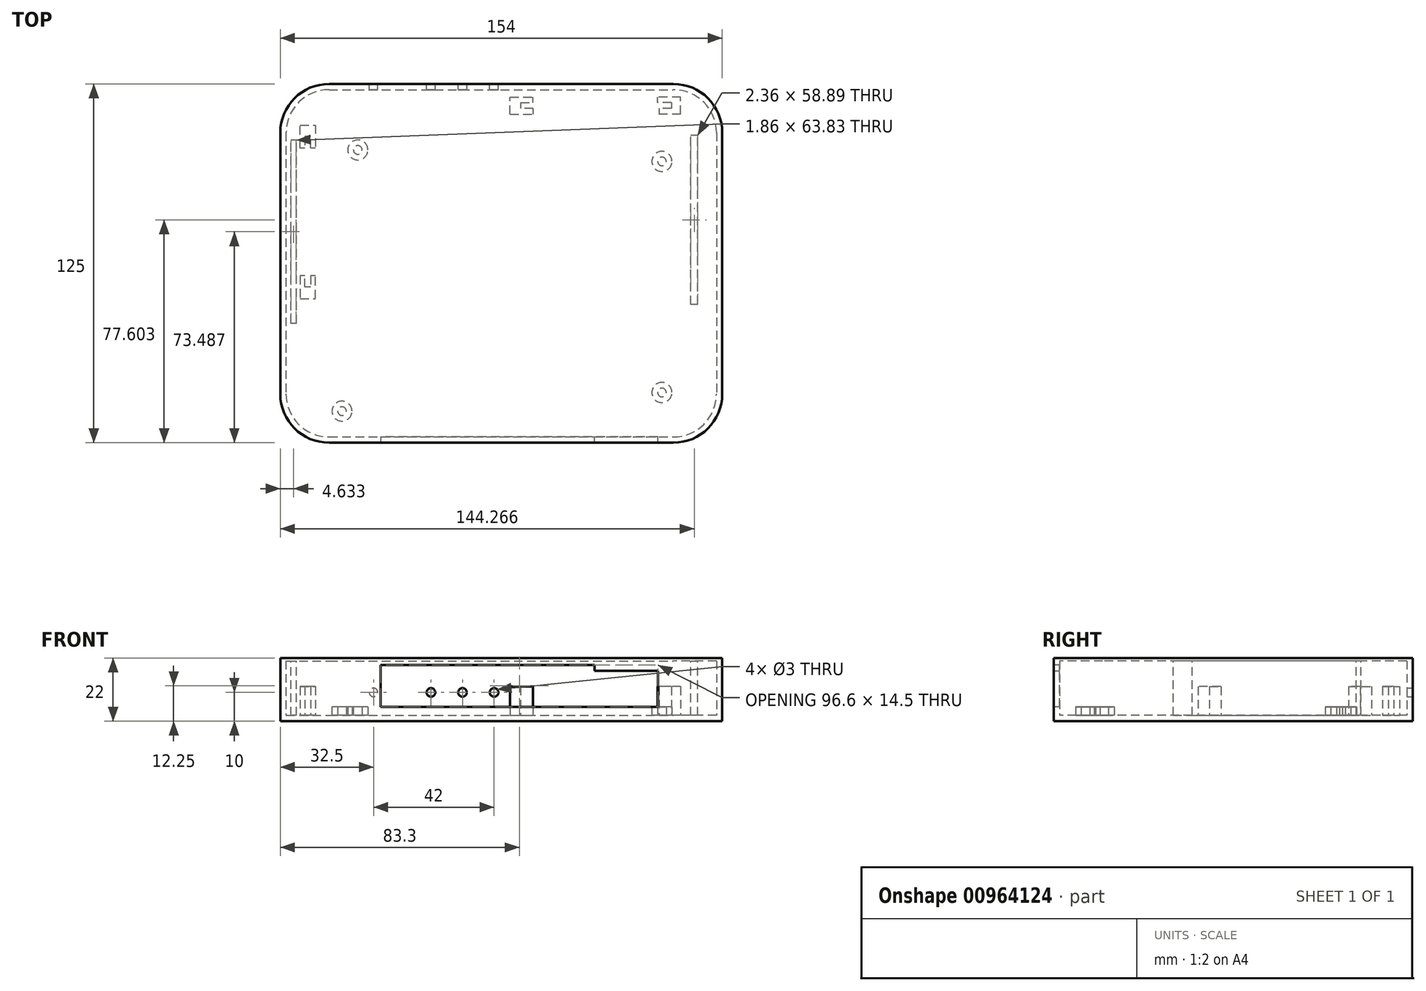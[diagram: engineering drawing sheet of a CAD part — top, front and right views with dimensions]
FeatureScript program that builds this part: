
annotation { "Feature Type Name" : "Feature", "Feature Type Description" : "" }
export const myFeature = defineFeature(function(context is Context, id is Id, definition is map)
    precondition{}
    {
        {
            var Q0;
            Q0=qCreatedBy(makeId("Top.planeOp"),FACE);
            var sketch = newSketch(context, id + "F0", { "sketchPlane" : qUnion([Q0])});
            skPoint(sketch, "E0.middle", {"position": v(0, 0) * mm});
            skLineSegment(sketch, "E1.bottom", {"start": v(-60, -55) * mm, "end": v(60, -55) * mm});
            skLineSegment(sketch, "E1.top", {"start": v(-60, 55) * mm, "end": v(60, 55) * mm});
            skLineSegment(sketch, "E1.left", {"start": v(-60, -55) * mm, "end": v(-60, 55) * mm});
            skLineSegment(sketch, "E1.right", {"start": v(60, -55) * mm, "end": v(60, 55) * mm});
            skPoint(sketch, "E2", {"position": v(-50, 45) * mm});
            skPoint(sketch, "E3", {"position": v(56, 41) * mm});
            skPoint(sketch, "E4", {"position": v(56, -39.5) * mm});
            skPoint(sketch, "E5", {"position": v(-55.5, -46) * mm});
            skCircle(sketch, "E6", {"center": v(-50, 45) * mm, "radius": 1.5 * mm});
            skCircle(sketch, "E7", {"center": v(56, 41) * mm, "radius": 1.5 * mm});
            skCircle(sketch, "E8", {"center": v(56, -39.5) * mm, "radius": 1.5 * mm});
            skCircle(sketch, "E9", {"center": v(-55.5, -46) * mm, "radius": 1.5 * mm});
            skLineSegment(sketch, "E10.bottom", {"start": v(-60, 66) * mm, "end": v(60, 66) * mm});
            skLineSegment(sketch, "E10.left", {"start": v(-75, 51) * mm, "end": v(-75, -40) * mm});
            skLineSegment(sketch, "E10.right", {"start": v(75, 51) * mm, "end": v(75, -40) * mm});
            skPoint(sketch, "E11.visualSharp", {"position": v(-75, -55) * mm});
            skArc(sketch, "E11.filletArc", {"start": v(-75, -40) * mm, "mid": v(-70.6, -50.6) * mm, "end": v(-60, -55) * mm});
            skPoint(sketch, "E12.visualSharp", {"position": v(75, 66) * mm});
            skArc(sketch, "E12.filletArc", {"start": v(75, 51) * mm, "mid": v(70.6, 61.6) * mm, "end": v(60, 66) * mm});
            skPoint(sketch, "E13.visualSharp", {"position": v(75, -55) * mm});
            skArc(sketch, "E13.filletArc", {"start": v(60, -55) * mm, "mid": v(70.6, -50.6) * mm, "end": v(75, -40) * mm});
            skPoint(sketch, "E14.visualSharp", {"position": v(-75, 66) * mm});
            skArc(sketch, "E14.filletArc", {"start": v(-60, 66) * mm, "mid": v(-70.6, 61.6) * mm, "end": v(-75, 51) * mm});
            skArc(sketch, "E15.0", {"start": v(-77, -40) * mm, "mid": v(-72.02, -52.02) * mm, "end": v(-60, -57) * mm});
            skLineSegment(sketch, "E15.1", {"start": v(-77, 51) * mm, "end": v(-77, -40) * mm});
            skLineSegment(sketch, "E15.2", {"start": v(-60, -57) * mm, "end": v(60, -57) * mm});
            skArc(sketch, "E15.3", {"start": v(-60, 68) * mm, "mid": v(-72.02, 63.02) * mm, "end": v(-77, 51) * mm});
            skArc(sketch, "E15.4", {"start": v(60, -57) * mm, "mid": v(72.02, -52.02) * mm, "end": v(77, -40) * mm});
            skLineSegment(sketch, "E15.5", {"start": v(77, 51) * mm, "end": v(77, -40) * mm});
            skArc(sketch, "E15.6", {"start": v(77, 51) * mm, "mid": v(72.02, 63.02) * mm, "end": v(60, 68) * mm});
            skLineSegment(sketch, "E15.7", {"start": v(-60, 68) * mm, "end": v(60, 68) * mm});
            skCircle(sketch, "E16", {"center": v(-50, 45) * mm, "radius": 3.5 * mm});
            skCircle(sketch, "E17", {"center": v(56, 41) * mm, "radius": 3.5 * mm});
            skCircle(sketch, "E18", {"center": v(56, -39.5) * mm, "radius": 3.5 * mm});
            skCircle(sketch, "E19", {"center": v(-55.5, -46) * mm, "radius": 3.5 * mm});
            skLineSegment(sketch, "E20.left", {"start": v(6.8, 61.48) * mm, "end": v(6.8, 59.48) * mm});
            skLineSegment(sketch, "E20.right", {"start": v(59.3, 61.48) * mm, "end": v(59.3, 59.48) * mm});
            skLineSegment(sketch, "E21.bottom", {"start": v(62.5, 57.48) * mm, "end": v(55, 57.48) * mm});
            skLineSegment(sketch, "E21.top", {"start": v(62.5, 63.48) * mm, "end": v(54.5, 63.48) * mm});
            skLineSegment(sketch, "E21.left", {"start": v(62.5, 57.48) * mm, "end": v(62.5, 63.48) * mm});
            skLineSegment(sketch, "E22.bottom", {"start": v(3.09, 57.48) * mm, "end": v(11.09, 57.48) * mm});
            skLineSegment(sketch, "E22.top", {"start": v(3.09, 63.48) * mm, "end": v(11.09, 63.48) * mm});
            skLineSegment(sketch, "E22.left", {"start": v(3.09, 57.48) * mm, "end": v(3.09, 63.48) * mm});
            skPoint(sketch, "E23", {"position": v(11.09, 61.48) * mm});
            skPoint(sketch, "E24", {"position": v(11.09, 59.48) * mm});
            skLineSegment(sketch, "E25", {"start": v(11.09, 59.48) * mm, "end": v(6.8, 59.48) * mm});
            skLineSegment(sketch, "E26", {"start": v(6.8, 59.48) * mm, "end": v(6.8, 61.48) * mm});
            skLineSegment(sketch, "E27", {"start": v(6.8, 61.48) * mm, "end": v(11.09, 61.48) * mm});
            skLineSegment(sketch, "E28", {"start": v(59.3, 59.48) * mm, "end": v(55, 59.48) * mm});
            skLineSegment(sketch, "E29", {"start": v(55, 59.48) * mm, "end": v(55, 57.48) * mm});
            skLineSegment(sketch, "E30", {"start": v(59.3, 61.48) * mm, "end": v(54.5, 61.48) * mm});
            skLineSegment(sketch, "E31", {"start": v(54.5, 61.48) * mm, "end": v(54.5, 63.48) * mm});
            skLineSegment(sketch, "E32", {"start": v(11.09, 61.48) * mm, "end": v(11.09, 63.48) * mm});
            skLineSegment(sketch, "E33", {"start": v(11.09, 59.48) * mm, "end": v(11.09, 57.48) * mm});
            skLineSegment(sketch, "E34", {"start": v(-70.08, 45.68) * mm, "end": v(-70.08, 53.68) * mm});
            skLineSegment(sketch, "E35", {"start": v(-70.08, 53.68) * mm, "end": v(-64.77, 53.68) * mm});
            skLineSegment(sketch, "E36", {"start": v(-64.77, 53.68) * mm, "end": v(-64.77, 45.68) * mm});
            skLineSegment(sketch, "E37", {"start": v(-64.77, 45.68) * mm, "end": v(-66.43, 45.68) * mm});
            skLineSegment(sketch, "E38", {"start": v(-66.43, 45.68) * mm, "end": v(-66.43, 49.68) * mm});
            skLineSegment(sketch, "E39", {"start": v(-66.43, 49.68) * mm, "end": v(-68.43, 49.68) * mm});
            skLineSegment(sketch, "E40", {"start": v(-68.43, 49.68) * mm, "end": v(-68.43, 45.68) * mm});
            skLineSegment(sketch, "E41", {"start": v(-68.43, 45.68) * mm, "end": v(-70.08, 45.68) * mm});
            skLineSegment(sketch, "E42", {"start": v(-72.56, 23.43) * mm, "end": v(-61.06, 23.43) * mm});
            skLineSegment(sketch, "E43.MirrorCS", {"start": v(-66.43, -2.82) * mm, "end": v(-68.43, -2.82) * mm});
            skLineSegment(sketch, "E44.MirrorCS", {"start": v(-64.77, 1.18) * mm, "end": v(-66.43, 1.18) * mm});
            skLineSegment(sketch, "E45.MirrorCS", {"start": v(-68.43, 1.18) * mm, "end": v(-70.08, 1.18) * mm});
            skLineSegment(sketch, "E46.MirrorCS", {"start": v(-70.08, 1.18) * mm, "end": v(-70.08, -6.82) * mm});
            skLineSegment(sketch, "E47.MirrorCS", {"start": v(-68.43, -2.82) * mm, "end": v(-68.43, 1.18) * mm});
            skLineSegment(sketch, "E48.MirrorCS", {"start": v(-70.08, -6.82) * mm, "end": v(-64.77, -6.82) * mm});
            skLineSegment(sketch, "E49.MirrorCS", {"start": v(-64.77, -6.82) * mm, "end": v(-64.77, 1.18) * mm});
            skLineSegment(sketch, "E50.MirrorCS", {"start": v(-66.43, 1.18) * mm, "end": v(-66.43, -2.82) * mm});
            skSolve(sketch);
        }
        {
            var Q0;
            Q0=makeQuery(id+"F0.imprint","IMPRINT",FACE,{"disambiguationData":[TD([[makeQuery(id+"F0.imprint","IMPRINT",EDGE,{"derivedFrom":sQuery(id+"F0.wireOp",EDGE,"E10.bottom")}),1.0]])]});
            var Q1;
            Q1=makeQuery(id+"F0.imprint","IMPRINT",FACE,{"disambiguationData":[TD([[makeQuery(id+"F0.imprint","IMPRINT",EDGE,{"derivedFrom":sQuery(id+"F0.wireOp",EDGE,"E1.top")}),-1.0]])]});
            var Q2;
            Q2=makeQuery(id+"F0.imprint","IMPRINT",FACE,{"disambiguationData":[TD([[makeQuery(id+"F0.imprint","IMPRINT",EDGE,{"derivedFrom":sQuery(id+"F0.wireOp",EDGE,"E1.top")}),1.0]])]});
            var Q3;
            Q3=makeQuery(id+"F0.imprint","IMPRINT",FACE,{"disambiguationData":[TD([[makeQuery(id+"F0.imprint","IMPRINT",EDGE,{"derivedFrom":sQuery(id+"F0.wireOp",EDGE,"E9")}),1.0]])]});
            var Q4;
            Q4=makeQuery(id+"F0.imprint","IMPRINT",FACE,{"disambiguationData":[TD([[makeQuery(id+"F0.imprint","IMPRINT",EDGE,{"derivedFrom":sQuery(id+"F0.wireOp",EDGE,"E7")}),1.0]])]});
            var Q5;
            Q5=makeQuery(id+"F0.imprint","IMPRINT",FACE,{"disambiguationData":[TD([[makeQuery(id+"F0.imprint","IMPRINT",EDGE,{"derivedFrom":sQuery(id+"F0.wireOp",EDGE,"E6")}),1.0]])]});
            var Q6;
            Q6=makeQuery(id+"F0.imprint","IMPRINT",FACE,{"disambiguationData":[TD([[makeQuery(id+"F0.imprint","IMPRINT",EDGE,{"derivedFrom":sQuery(id+"F0.wireOp",EDGE,"E8")}),1.0]])]});
            var Q7;
            Q7=makeQuery(id+"F0.imprint","IMPRINT",FACE,{"disambiguationData":[TD([[makeQuery(id+"F0.imprint","IMPRINT",EDGE,{"derivedFrom":sQuery(id+"F0.wireOp",EDGE,"E8")}),-1.0]])]});
            var Q8;
            Q8=makeQuery(id+"F0.imprint","IMPRINT",FACE,{"disambiguationData":[TD([[makeQuery(id+"F0.imprint","IMPRINT",EDGE,{"derivedFrom":sQuery(id+"F0.wireOp",EDGE,"E6")}),-1.0]])]});
            var Q9;
            Q9=makeQuery(id+"F0.imprint","IMPRINT",FACE,{"disambiguationData":[TD([[makeQuery(id+"F0.imprint","IMPRINT",EDGE,{"derivedFrom":sQuery(id+"F0.wireOp",EDGE,"E7")}),-1.0]])]});
            var Q10;
            Q10=makeQuery(id+"F0.imprint","IMPRINT",FACE,{"disambiguationData":[TD([[makeQuery(id+"F0.imprint","IMPRINT",EDGE,{"derivedFrom":sQuery(id+"F0.wireOp",EDGE,"E9")}),-1.0]])]});
            var Q11;
            Q11=makeQuery(id+"F0.imprint","IMPRINT",FACE,{"disambiguationData":[TD([[makeQuery(id+"F0.imprint","IMPRINT",EDGE,{"derivedFrom":sQuery(id+"F0.wireOp",EDGE,"E22.bottom")}),1.0]])]});
            var Q12;
            Q12=makeQuery(id+"F0.imprint","IMPRINT",FACE,{"disambiguationData":[TD([[makeQuery(id+"F0.imprint","IMPRINT",EDGE,{"derivedFrom":sQuery(id+"F0.wireOp",EDGE,"E20.right")}),1.0]])]});
            var Q13;
            Q13=makeQuery(id+"F0.imprint","IMPRINT",FACE,{"disambiguationData":[TD([[makeQuery(id+"F0.imprint","IMPRINT",EDGE,{"derivedFrom":sQuery(id+"F0.wireOp",EDGE,"E34")}),-1.0]])]});
            var Q14;
            Q14=makeQuery(id+"F0.imprint","IMPRINT",FACE,{"disambiguationData":[TD([[makeQuery(id+"F0.imprint","IMPRINT",EDGE,{"derivedFrom":sQuery(id+"F0.wireOp",EDGE,"E43.MirrorCS")}),1.0]])]});
            extrude(context, id + "F1", {"entities" : qUnion([Q0, Q1, Q2, Q3, Q4, Q5, Q6, Q7, Q8, Q9, Q10, Q11, Q12, Q13, Q14]), "oppositeDirection" : true, "depth" : 2 * mm, "offsetDistance" : 25 * mm});
        }
        {
            var Q0;
            Q0 = qSketchRegion(id + "F0", true);
            extrude(context, id + "F2", {"entities" : qUnion([Q0]), "operationType" : NewBodyOperationType.ADD, "depth" : 20 * mm, "offsetDistance" : 25 * mm});
        }
        {
            var Q0;
            Q0=makeQuery(id+"F0.imprint","IMPRINT",FACE,{"disambiguationData":[TD([[makeQuery(id+"F0.imprint","IMPRINT",EDGE,{"derivedFrom":sQuery(id+"F0.wireOp",EDGE,"E6")}),-1.0]])]});
            var Q1;
            Q1=makeQuery(id+"F0.imprint","IMPRINT",FACE,{"disambiguationData":[TD([[makeQuery(id+"F0.imprint","IMPRINT",EDGE,{"derivedFrom":sQuery(id+"F0.wireOp",EDGE,"E7")}),-1.0]])]});
            var Q2;
            Q2=makeQuery(id+"F0.imprint","IMPRINT",FACE,{"disambiguationData":[TD([[makeQuery(id+"F0.imprint","IMPRINT",EDGE,{"derivedFrom":sQuery(id+"F0.wireOp",EDGE,"E8")}),-1.0]])]});
            var Q3;
            Q3=makeQuery(id+"F0.imprint","IMPRINT",FACE,{"disambiguationData":[TD([[makeQuery(id+"F0.imprint","IMPRINT",EDGE,{"derivedFrom":sQuery(id+"F0.wireOp",EDGE,"E9")}),-1.0]])]});
            extrude(context, id + "F3", {"entities" : qUnion([Q0, Q1, Q2, Q3]), "operationType" : NewBodyOperationType.ADD, "depth" : 3 * mm, "offsetDistance" : 25 * mm});
        }
        {
            var Q0;
            Q0=makeQuery(id+"F0.imprint","IMPRINT",FACE,{"disambiguationData":[TD([[makeQuery(id+"F0.imprint","IMPRINT",EDGE,{"derivedFrom":sQuery(id+"F0.wireOp",EDGE,"E22.bottom")}),1.0]])]});
            var Q1;
            Q1=makeQuery(id+"F0.imprint","IMPRINT",FACE,{"disambiguationData":[TD([[makeQuery(id+"F0.imprint","IMPRINT",EDGE,{"derivedFrom":sQuery(id+"F0.wireOp",EDGE,"E20.right")}),1.0]])]});
            var Q2;
            Q2=makeQuery(id+"F0.imprint","IMPRINT",FACE,{"disambiguationData":[TD([[makeQuery(id+"F0.imprint","IMPRINT",EDGE,{"derivedFrom":sQuery(id+"F0.wireOp",EDGE,"E43.MirrorCS")}),1.0]])]});
            var Q3;
            Q3=makeQuery(id+"F0.imprint","IMPRINT",FACE,{"disambiguationData":[TD([[makeQuery(id+"F0.imprint","IMPRINT",EDGE,{"derivedFrom":sQuery(id+"F0.wireOp",EDGE,"E34")}),-1.0]])]});
            extrude(context, id + "F4", {"entities" : qUnion([Q0, Q1, Q2, Q3]), "operationType" : NewBodyOperationType.ADD, "depth" : 10 * mm, "offsetDistance" : 25 * mm});
        }
        {
            var Q0;
            Q0=makeQuery(id+"F2.opExtrude","CAP_FACE",FACE,{"disambiguationData":[OSD([sQuery(id+"F0.wireOp",EDGE,"E10.bottom"),sQuery(id+"F0.wireOp",EDGE,"E1.bottom"),sQuery(id+"F0.wireOp",EDGE,"E10.left"),sQuery(id+"F0.wireOp",EDGE,"E10.right"),sQuery(id+"F0.wireOp",EDGE,"E11.filletArc"),sQuery(id+"F0.wireOp",EDGE,"E12.filletArc"),sQuery(id+"F0.wireOp",EDGE,"E13.filletArc"),sQuery(id+"F0.wireOp",EDGE,"E14.filletArc"),sQuery(id+"F0.wireOp",EDGE,"E15.0"),sQuery(id+"F0.wireOp",EDGE,"E15.1"),sQuery(id+"F0.wireOp",EDGE,"E15.2"),sQuery(id+"F0.wireOp",EDGE,"E15.3"),sQuery(id+"F0.wireOp",EDGE,"E15.4"),sQuery(id+"F0.wireOp",EDGE,"E15.5"),sQuery(id+"F0.wireOp",EDGE,"E15.6"),sQuery(id+"F0.wireOp",EDGE,"E15.7")])],"isStart":false});
            var sketch = newSketch(context, id + "F5", { "sketchPlane" : qUnion([Q0])});
            skLineSegment(sketch, "E51.left", {"start": v(-42, -55) * mm, "end": v(-42, -57) * mm});
            skLineSegment(sketch, "E52.left", {"start": v(54.6, -57) * mm, "end": v(54.6, -55) * mm});
            skLineSegment(sketch, "E53", {"start": v(-42, -55) * mm, "end": v(54.6, -55) * mm});
            skLineSegment(sketch, "E54", {"start": v(54.6, -57) * mm, "end": v(-42, -57) * mm});
            skSolve(sketch);
        }
        {
            var Q0;
            Q0=makeQuery(id+"F5.imprint","IMPRINT",FACE,{"disambiguationData":[TD([[makeQuery(id+"F5.imprint","IMPRINT",EDGE,{"derivedFrom":sQuery(id+"F5.wireOp",EDGE,"E51.left")}),1.0]])]});
            var Q1;
            Q1=makeQuery(id+"F1.opExtrude","SWEPT_BODY",BODY,{"disambiguationData":[OSD([sQuery(id+"F0.wireOp",EDGE,"E15.0"),sQuery(id+"F0.wireOp",EDGE,"E15.1"),sQuery(id+"F0.wireOp",EDGE,"E15.2"),sQuery(id+"F0.wireOp",EDGE,"E15.3"),sQuery(id+"F0.wireOp",EDGE,"E15.4"),sQuery(id+"F0.wireOp",EDGE,"E15.5"),sQuery(id+"F0.wireOp",EDGE,"E15.6"),sQuery(id+"F0.wireOp",EDGE,"E15.7")])]});
            extrude(context, id + "F6", {"entities" : qUnion([Q0]), "operationType" : NewBodyOperationType.REMOVE, "endBound" : BoundingType.UP_TO_BODY, "oppositeDirection" : true, "depth" : 25 * mm, "endBoundEntityBody" : qUnion([Q1]), "hasOffset" : true, "offsetDistance" : 5 * mm});
        }
        {
            var Q0;
            {var subQ0=sQuery(id+"F0.wireOp",EDGE,"E15.7");Q0=makeQuery(id+"F2.boolean.opBoolean","MERGE",FACE,{"derivedFrom":[makeQuery(id+"F1.opExtrude","SWEPT_FACE",FACE,{"disambiguationData":[OSD([subQ0])]}),makeQuery(id+"F2.opExtrude","SWEPT_FACE",FACE,{"disambiguationData":[OSD([subQ0])]})]});}
            var sketch = newSketch(context, id + "F7", { "sketchPlane" : qUnion([Q0])});
            skPoint(sketch, "E55", {"position": v(44.5, 8) * mm});
            skPoint(sketch, "E56", {"position": v(24.5, 8) * mm});
            skPoint(sketch, "E57", {"position": v(13.5, 8) * mm});
            skPoint(sketch, "E58", {"position": v(2.5, 8) * mm});
            skCircle(sketch, "E59", {"center": v(2.5, 8) * mm, "radius": 1.5 * mm});
            skCircle(sketch, "E60", {"center": v(13.5, 8) * mm, "radius": 1.5 * mm});
            skCircle(sketch, "E61", {"center": v(24.5, 8) * mm, "radius": 1.5 * mm});
            skCircle(sketch, "E62", {"center": v(44.5, 8) * mm, "radius": 1.5 * mm});
            skSolve(sketch);
        }
        {
            var Q0;
            Q0=makeQuery(id+"F7.imprint","IMPRINT",FACE,{"disambiguationData":[TD([[makeQuery(id+"F7.imprint","IMPRINT",EDGE,{"derivedFrom":sQuery(id+"F7.wireOp",EDGE,"E59")}),1.0]])]});
            var Q1;
            Q1=makeQuery(id+"F7.imprint","IMPRINT",FACE,{"disambiguationData":[TD([[makeQuery(id+"F7.imprint","IMPRINT",EDGE,{"derivedFrom":sQuery(id+"F7.wireOp",EDGE,"E60")}),1.0]])]});
            var Q2;
            Q2=makeQuery(id+"F7.imprint","IMPRINT",FACE,{"disambiguationData":[TD([[makeQuery(id+"F7.imprint","IMPRINT",EDGE,{"derivedFrom":sQuery(id+"F7.wireOp",EDGE,"E61")}),1.0]])]});
            var Q3;
            Q3=makeQuery(id+"F7.imprint","IMPRINT",FACE,{"disambiguationData":[TD([[makeQuery(id+"F7.imprint","IMPRINT",EDGE,{"derivedFrom":sQuery(id+"F7.wireOp",EDGE,"E62")}),1.0]])]});
            extrude(context, id + "F8", {"entities" : qUnion([Q0, Q1, Q2, Q3]), "operationType" : NewBodyOperationType.REMOVE, "endBound" : BoundingType.UP_TO_NEXT, "oppositeDirection" : true, "depth" : 25 * mm, "offsetDistance" : 25 * mm});
        }
        {
            var Q0;
            Q0=makeQuery(id+"F2.opExtrude","CAP_FACE",FACE,{"disambiguationData":[OSD([sQuery(id+"F0.wireOp",EDGE,"E10.bottom"),sQuery(id+"F0.wireOp",EDGE,"E1.bottom"),sQuery(id+"F0.wireOp",EDGE,"E10.left"),sQuery(id+"F0.wireOp",EDGE,"E10.right"),sQuery(id+"F0.wireOp",EDGE,"E11.filletArc"),sQuery(id+"F0.wireOp",EDGE,"E12.filletArc"),sQuery(id+"F0.wireOp",EDGE,"E13.filletArc"),sQuery(id+"F0.wireOp",EDGE,"E14.filletArc"),sQuery(id+"F0.wireOp",EDGE,"E15.0"),sQuery(id+"F0.wireOp",EDGE,"E15.1"),sQuery(id+"F0.wireOp",EDGE,"E15.2"),sQuery(id+"F0.wireOp",EDGE,"E15.3"),sQuery(id+"F0.wireOp",EDGE,"E15.4"),sQuery(id+"F0.wireOp",EDGE,"E15.5"),sQuery(id+"F0.wireOp",EDGE,"E15.6"),sQuery(id+"F0.wireOp",EDGE,"E15.7")])],"isStart":false});
            var sketch = newSketch(context, id + "F9", { "sketchPlane" : qUnion([Q0])});
            skLineSegment(sketch, "E63", {"start": v(-75, -40) * mm, "end": v(-75, 51) * mm});
            skArc(sketch, "E64", {"start": v(-75, 51) * mm, "mid": v(-70.6, 61.6) * mm, "end": v(-60, 66) * mm});
            skArc(sketch, "E65", {"start": v(60, 66) * mm, "mid": v(70.6, 61.6) * mm, "end": v(75, 51) * mm});
            skArc(sketch, "E66", {"start": v(75, -40) * mm, "mid": v(70.6, -50.6) * mm, "end": v(60, -55) * mm});
            skArc(sketch, "E67", {"start": v(-60, -55) * mm, "mid": v(-70.6, -50.6) * mm, "end": v(-75, -40) * mm});
            skLineSegment(sketch, "E68", {"start": v(-60, 66) * mm, "end": v(60, 66) * mm});
            skLineSegment(sketch, "E69", {"start": v(75, 51) * mm, "end": v(75, -40) * mm});
            skLineSegment(sketch, "E70", {"start": v(60, -55) * mm, "end": v(54.6, -55) * mm});
            skLineSegment(sketch, "E71", {"start": v(54.6, -55) * mm, "end": v(54.6, -57) * mm});
            skLineSegment(sketch, "E72", {"start": v(-42, -57) * mm, "end": v(-42, -55) * mm});
            skLineSegment(sketch, "E73", {"start": v(-42, -55) * mm, "end": v(-60, -55) * mm});
            skLineSegment(sketch, "E74", {"start": v(-42, -55) * mm, "end": v(32.5, -55) * mm});
            skLineSegment(sketch, "E75", {"start": v(-42, -57) * mm, "end": v(32.5, -57) * mm});
            skLineSegment(sketch, "E76", {"start": v(32.5, -57) * mm, "end": v(54.6, -57) * mm});
            skLineSegment(sketch, "E77", {"start": v(32.5, -55) * mm, "end": v(54.6, -55) * mm});
            skLineSegment(sketch, "E78", {"start": v(32.5, -57) * mm, "end": v(32.5, -55) * mm});
            skLineSegment(sketch, "E79.bottom", {"start": v(-73.3, 48.4) * mm, "end": v(-71.44, 48.4) * mm});
            skLineSegment(sketch, "E79.top", {"start": v(-73.3, -15.43) * mm, "end": v(-71.44, -15.43) * mm});
            skLineSegment(sketch, "E79.left", {"start": v(-73.3, 48.4) * mm, "end": v(-73.3, -15.43) * mm});
            skLineSegment(sketch, "E79.right", {"start": v(-71.44, 48.4) * mm, "end": v(-71.44, -15.43) * mm});
            skLineSegment(sketch, "E80.bottom", {"start": v(66.09, 50.05) * mm, "end": v(68.44, 50.05) * mm});
            skLineSegment(sketch, "E80.top", {"start": v(66.09, -8.84) * mm, "end": v(68.44, -8.84) * mm});
            skLineSegment(sketch, "E80.left", {"start": v(66.09, 50.05) * mm, "end": v(66.09, -8.84) * mm});
            skLineSegment(sketch, "E80.right", {"start": v(68.44, 50.05) * mm, "end": v(68.44, -8.84) * mm});
            skSolve(sketch);
        }
        {
            var Q0;
            Q0=makeQuery(id+"F9.imprint","IMPRINT",FACE,{"disambiguationData":[TD([[makeQuery(id+"F9.imprint","IMPRINT",EDGE,{"derivedFrom":sQuery(id+"F9.wireOp",EDGE,"E63")}),1.0]])]});
            extrude(context, id + "F10", {"entities" : qUnion([Q0]), "oppositeDirection" : true, "depth" : 1 * mm, "offsetDistance" : 25 * mm});
        }
        {
            var Q0;
            Q0=makeQuery(id+"F9.imprint","IMPRINT",FACE,{"disambiguationData":[TD([[makeQuery(id+"F9.imprint","IMPRINT",EDGE,{"derivedFrom":sQuery(id+"F9.wireOp",EDGE,"E72")}),1.0]])]});
            extrude(context, id + "F11", {"entities" : qUnion([Q0]), "operationType" : NewBodyOperationType.ADD, "oppositeDirection" : true, "depth" : 2.5 * mm, "offsetDistance" : 25 * mm});
        }
        {
            var Q0;
            Q0=makeQuery(id+"F9.imprint","IMPRINT",FACE,{"disambiguationData":[TD([[makeQuery(id+"F9.imprint","IMPRINT",EDGE,{"derivedFrom":sQuery(id+"F9.wireOp",EDGE,"E71")}),1.0]])]});
            extrude(context, id + "F12", {"entities" : qUnion([Q0]), "operationType" : NewBodyOperationType.ADD, "oppositeDirection" : true, "depth" : 4.5 * mm, "offsetDistance" : 25 * mm});
        }
        {
            var Q0;
            Q0=makeQuery(id+"F9.imprint","IMPRINT",FACE,{"disambiguationData":[TD([[makeQuery(id+"F9.imprint","IMPRINT",EDGE,{"derivedFrom":sQuery(id+"F9.wireOp",EDGE,"E79.bottom")}),-1.0]])]});
            var Q1;
            Q1=makeQuery(id+"F9.imprint","IMPRINT",FACE,{"disambiguationData":[TD([[makeQuery(id+"F9.imprint","IMPRINT",EDGE,{"derivedFrom":sQuery(id+"F9.wireOp",EDGE,"E80.bottom")}),-1.0]])]});
            var Q2;
            Q2=makeQuery(id+"F3.boolean.opBoolean","SPLIT",FACE,{"disambiguationData":[TD([makeQuery(id+"F2.opExtrude","SWEPT_FACE",FACE,{"disambiguationData":[OSD([sQuery(id+"F0.wireOp",EDGE,"E10.bottom")])]})])],"derivedFrom":makeQuery(id+"F1.opExtrude","CAP_FACE",FACE,{"disambiguationData":[OSD([sQuery(id+"F0.wireOp",EDGE,"E15.0"),sQuery(id+"F0.wireOp",EDGE,"E15.1"),sQuery(id+"F0.wireOp",EDGE,"E15.2"),sQuery(id+"F0.wireOp",EDGE,"E15.3"),sQuery(id+"F0.wireOp",EDGE,"E15.4"),sQuery(id+"F0.wireOp",EDGE,"E15.5"),sQuery(id+"F0.wireOp",EDGE,"E15.6"),sQuery(id+"F0.wireOp",EDGE,"E15.7")])],"isStart":true})});
            extrude(context, id + "F13", {"entities" : qUnion([Q0, Q1]), "operationType" : NewBodyOperationType.ADD, "endBound" : BoundingType.UP_TO_SURFACE, "oppositeDirection" : true, "depth" : 25 * mm, "endBoundEntityFace" : qUnion([Q2]), "offsetDistance" : 25 * mm});
        }
    });
